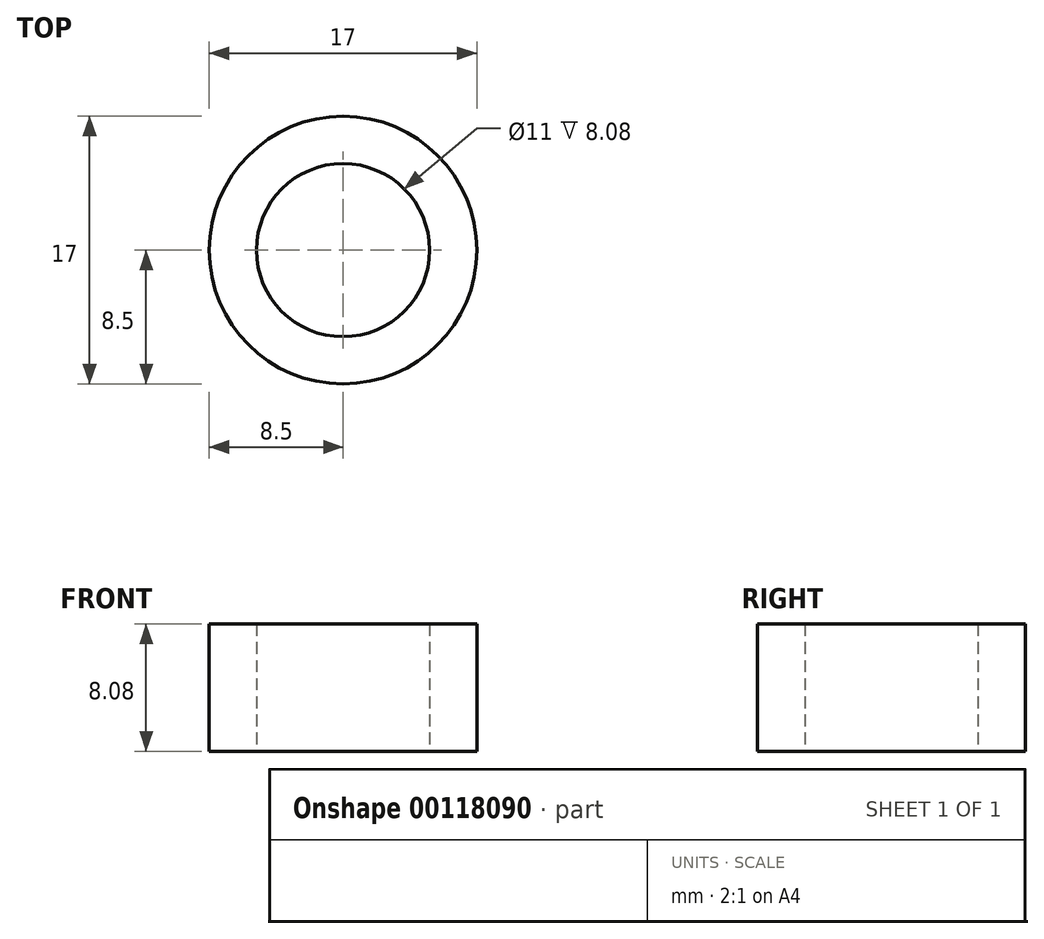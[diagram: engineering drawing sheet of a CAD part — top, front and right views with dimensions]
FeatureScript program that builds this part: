
annotation { "Feature Type Name" : "Feature", "Feature Type Description" : "" }
export const myFeature = defineFeature(function(context is Context, id is Id, definition is map)
    precondition{}
    {
        {
            var Q0;
            Q0=qCreatedBy(makeId("Top.planeOp"),FACE);
            var sketch = newSketch(context, id + "F0", { "sketchPlane" : qUnion([Q0])});
            skCircle(sketch, "E0", {"center": v(0, 0) * mm, "radius": 8.5 * mm});
            skCircle(sketch, "E1", {"center": v(0, 0) * mm, "radius": 5.5 * mm});
            skSolve(sketch);
        }
        {
            var Q0;
            Q0=makeQuery(id+"F0.imprint","IMPRINT",FACE,{"disambiguationData":[TD([[makeQuery(id+"F0.imprint","IMPRINT",EDGE,{"derivedFrom":sQuery(id+"F0.wireOp",EDGE,"E0")}),1.0]])]});
            extrude(context, id + "F1", {"entities" : qUnion([Q0]), "depth" : (22.08 - 14) * mm});
        }
    });
